# Revit family: IS_Strada_Multiproduct_BIM_GB_K0781;K0816
name_source: partatom
category: Plumbing Fixtures
revit_build: Autodesk Revit MEP 2014 (Build: 20130308_1515(x64)
units: mm (PartAtom-declared; Revit-internal decimal feet)

## types (2) — shared parameters
Accessories = www.idealspec.co.uk
AreaUnits = millimeters
Assembly Code = C1030220
AssetType = Fixed
BREEAM = No
BasinMaterial = ISI_IdealStandard_Sanitaryware_White6_Render
Brand = Ideal Standard
Category = SanitaryTerminal_WASHHANDBASIN_UK
Color = White
ConnectionType = Plumbing
DrainSize = 32 mm  [stored 0.104987 ft]
DurationUnit = year
ECA = No
ExpectedLife = 30
Finish = White
IfcExportAs = IfcSanitaryTerminalType
IfcExportType = WASHHANDBASIN
InstallationInstructions = www.idealspec.co.uk/resources.html
LinearUnits = millimeters
ManufacturerURL = www.idealspec.co.uk
Material = Vitreous china
NBSDescription = Counter top washbasins
NBSReference = 45-35-70/360
NettWeight = 13 Kg
NominalHeight = 130 mm  [stored 0.426509 ft]
NominalWidth = 420 mm
OneTH = Yes
Shape = Rectangular
Space = Internal
SpareParts = www.fastpart-spares.co.uk
TMV3 = No
URL = www.idealspec.co.uk
Uniclass2 = Pr_40_20_96_18
Version = 2
VolumeUnits = Litres
WRAS = No
WarrantyDescription = Manufacturers Warranty
WarrantyDurationParts = 99
WarrantyDurationUnit = year
WashHandBasinMounting = CounterTop
WashHandBasinType = HandRinse
WasteCentreLine = 210 mm
WaterEfficientProduct = No
zero-valued in all types: CWFU, Default Elevation, HWFU, WFU

## per-type parameters (varying)
| type | BIMObjectName | Description | Features | Model | ModelNumber | ModelReference | Name | NominalDepth | NominalLength | ProductInformation | Size |
| K081601 - Strada 50cm vessel washbasin, 1 taphole, glazed back with overflow | ISI_IdealStandard_CounterTopWashbasins_Strada_K0816 | Strada 50cm vessel washbasin, 1 taphole, glazed back with overflow | 50cm vessel washbasin, 1 taphole, glazed back with overflow | K081601 | K081601 | Strada 50cm vessel washbasin, 1 taphole, glazed back with overflow | CounterTopWashBasins_Strada_K0816_IdealStandard | 500 mm | 500 mm | www.idealspec.co.uk/assets/datasheet/K081601 | 500 x 420 x 150 mm |
| K078101 - Strada 60cm vessel washbasin, 1 taphole, glazed back with overflow | ISI_IdealStandard_CounterTopWashbasins_Strada_K0781 | Strada 60cm vessel washbasin, 1 taphole, glazed back with overflow | 60cm vessel washbasin, 1 taphole, glazed back with overflow | K078101 | K078101 | Strada 60cm vessel washbasin, 1 taphole, glazed back with overflow | CounterTopWashBasins_Strada_K0781_IdealStandard | 600 mm  [stored 1.9685 ft] | 600 mm  [stored 1.9685 ft] | www.idealspec.co.uk/assets/datasheet/K078101 | 600 x 420 x 150 mm |

note: [stored X ft] marks values corroborated as IEEE doubles in the binary element streams (Revit-internal decimal feet)

## geometry (parser evidence)
native form markers: Blend x2, Sweep x6
no freeform markers — native parametric forms only
